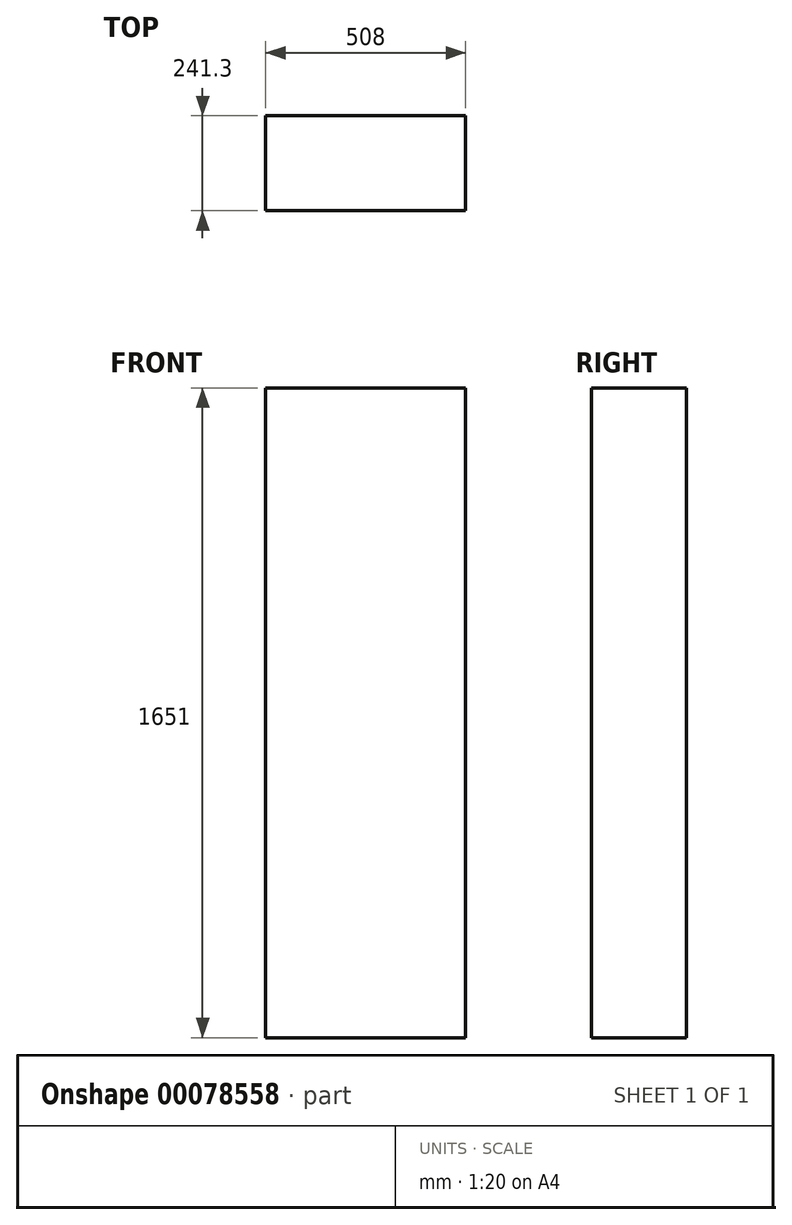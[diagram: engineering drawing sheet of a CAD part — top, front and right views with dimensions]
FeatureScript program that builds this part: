
annotation { "Feature Type Name" : "Feature", "Feature Type Description" : "" }
export const myFeature = defineFeature(function(context is Context, id is Id, definition is map)
    precondition{}
    {
        {
            var Q0;
            Q0=qCreatedBy(makeId("Top.planeOp"),FACE);
            var sketch = newSketch(context, id + "F0", { "sketchPlane" : qUnion([Q0])});
            skLineSegment(sketch, "E0.bottom", {"start": v(-338.35, 81.46) * mm, "end": v(169.65, 81.46) * mm});
            skLineSegment(sketch, "E0.top", {"start": v(-338.35, -159.84) * mm, "end": v(169.65, -159.84) * mm});
            skLineSegment(sketch, "E0.left", {"start": v(-338.35, 81.46) * mm, "end": v(-338.35, -159.84) * mm});
            skLineSegment(sketch, "E0.right", {"start": v(169.65, 81.46) * mm, "end": v(169.65, -159.84) * mm});
            skSolve(sketch);
        }
        {
            var Q0;
            Q0=makeQuery(id+"F0.imprint","IMPRINT",FACE,{"disambiguationData":[TD([[makeQuery(id+"F0.imprint","IMPRINT",EDGE,{"derivedFrom":sQuery(id+"F0.wireOp",EDGE,"E0.bottom")}),-1.0]])]});
            extrude(context, id + "F1", {"entities" : qUnion([Q0]), "depth" : 1651 * mm});
        }
    });
